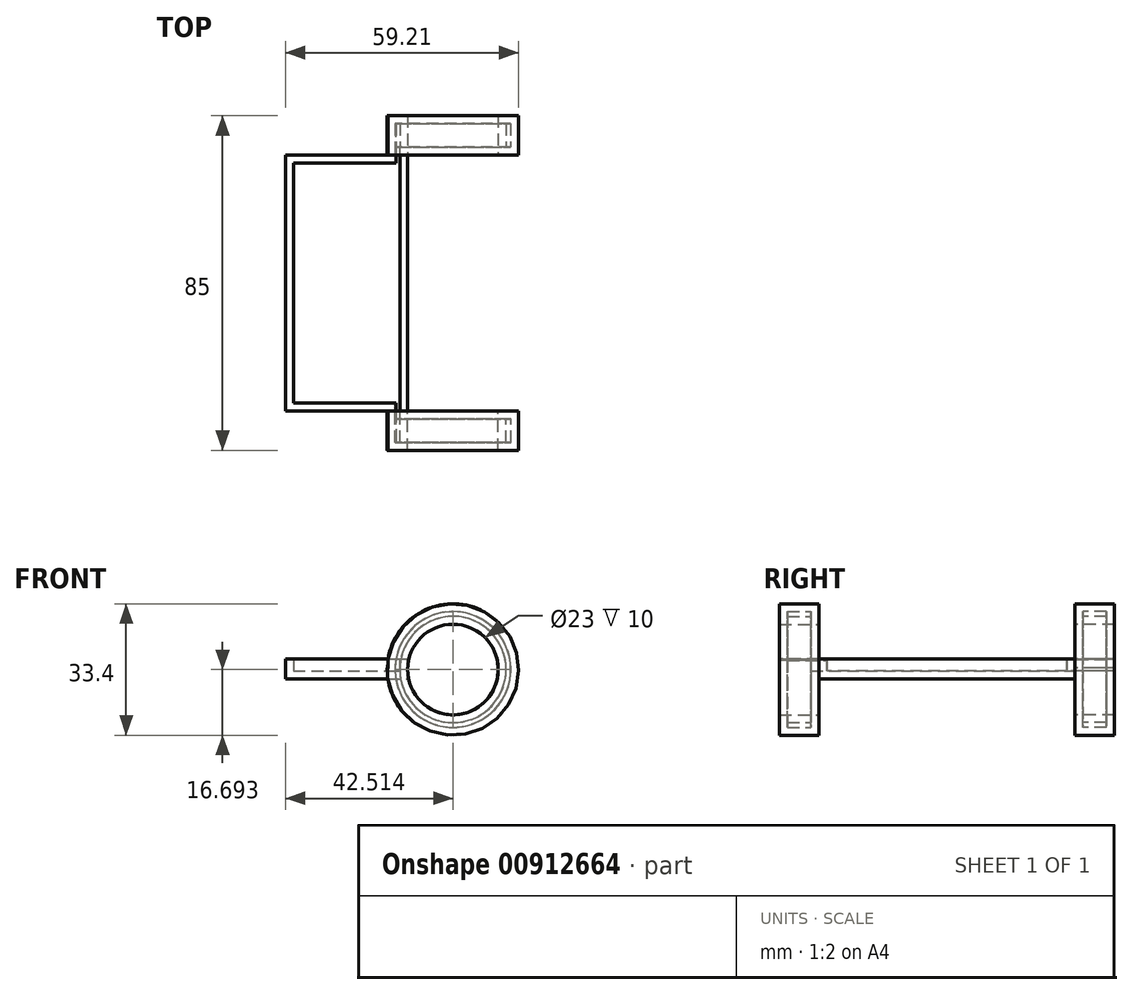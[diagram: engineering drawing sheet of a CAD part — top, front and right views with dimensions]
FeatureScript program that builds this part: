
annotation { "Feature Type Name" : "Feature", "Feature Type Description" : "" }
export const myFeature = defineFeature(function(context is Context, id is Id, definition is map)
    precondition{}
    {
        {
            var Q0;
            Q0=qCreatedBy(makeId("Top.planeOp"),FACE);
            var sketch = newSketch(context, id + "F0", { "sketchPlane" : qUnion([Q0])});
            skLineSegment(sketch, "E0.bottom", {"start": v(-43.57, 32.5) * mm, "end": v(-12.57, 32.5) * mm});
            skLineSegment(sketch, "E0.top", {"start": v(-43.57, -32.5) * mm, "end": v(-12.57, -32.5) * mm});
            skLineSegment(sketch, "E0.left", {"start": v(-43.57, 32.5) * mm, "end": v(-43.57, -32.5) * mm});
            skLineSegment(sketch, "E0.right", {"start": v(-12.57, 32.5) * mm, "end": v(-12.57, -32.5) * mm});
            skLineSegment(sketch, "E1.bottom", {"start": v(-12.57, -32.5) * mm, "end": v(-17.57, -32.5) * mm});
            skLineSegment(sketch, "E1.top", {"start": v(-12.57, -42.5) * mm, "end": v(-17.57, -42.5) * mm});
            skLineSegment(sketch, "E1.left", {"start": v(-12.57, -32.5) * mm, "end": v(-12.57, -42.5) * mm});
            skLineSegment(sketch, "E1.right", {"start": v(-17.57, -32.5) * mm, "end": v(-17.57, -42.5) * mm});
            skLineSegment(sketch, "E2.bottom", {"start": v(-12.57, 32.5) * mm, "end": v(-17.57, 32.5) * mm});
            skLineSegment(sketch, "E2.top", {"start": v(-12.57, 42.5) * mm, "end": v(-17.57, 42.5) * mm});
            skLineSegment(sketch, "E2.left", {"start": v(-12.57, 32.5) * mm, "end": v(-12.57, 42.5) * mm});
            skLineSegment(sketch, "E2.right", {"start": v(-17.57, 32.5) * mm, "end": v(-17.57, 42.5) * mm});
            skLineSegment(sketch, "E3", {"start": v(-43.57, 0) * mm, "end": v(-65.23, 0) * mm});
            skLineSegment(sketch, "E4", {"start": v(-17.57, 32.5) * mm, "end": v(-12.57, 32.5) * mm});
            skLineSegment(sketch, "E5", {"start": v(-17.57, -32.5) * mm, "end": v(-12.57, -32.5) * mm});
            skSolve(sketch);
        }
        {
            var Q0;
            Q0 = qSketchRegion(id + "F0", true);
            var Q1;
            Q1=makeQuery(id+"F0.imprint","IMPRINT",FACE,{"disambiguationData":[TD([[makeQuery(id+"F0.imprint","IMPRINT",EDGE,{"derivedFrom":sQuery(id+"F0.wireOp",EDGE,"E0.bottom")}),-1.0]])]});
            extrude(context, id + "F1", {"entities" : qUnion([Q0, Q1]), "depth" : 5 * mm, "offsetDistance" : 25.4 * mm});
        }
        {
            var Q0;
            Q0=qCreatedBy(makeId("Front.planeOp"),FACE);
            cPlane(context, id + "F2", {"entities" : qUnion([Q0]), "cplaneType" : CPlaneType.OFFSET, "offset" : 32.5 * mm, "width" : 152.4 * mm, "height" : 152.4 * mm});
        }
        {
            var Q0;
            Q0=qCreatedBy(makeId("Front.planeOp"),FACE);
            cPlane(context, id + "F3", {"entities" : qUnion([Q0]), "cplaneType" : CPlaneType.OFFSET, "offset" : 32.5 * mm, "oppositeDirection" : true, "width" : 152.4 * mm, "height" : 152.4 * mm});
        }
        {
            var Q0;
            Q0=qCreatedBy(id+"F3.planeOp",FACE);
            var sketch = newSketch(context, id + "F4", { "sketchPlane" : qUnion([Q0])});
            skCircle(sketch, "E6", {"center": v(-1.07, 2.34) * mm, "radius": 16.7 * mm});
            skCircle(sketch, "E7", {"center": v(-1.07, 2.34) * mm, "radius": 11.5 * mm});
            skSolve(sketch);
        }
        {
            var Q0;
            Q0 = qSketchRegion(id + "F4", true);
            extrude(context, id + "F5", {"entities" : qUnion([Q0]), "operationType" : NewBodyOperationType.ADD, "oppositeDirection" : true, "depth" : 10 * mm, "offsetDistance" : 25.4 * mm});
        }
        {
            var Q0;
            Q0=qCreatedBy(id+"F2.planeOp",FACE);
            var sketch = newSketch(context, id + "F6", { "sketchPlane" : qUnion([Q0])});
            skCircle(sketch, "E8", {"center": v(-1.06, 2.33) * mm, "radius": 11.5 * mm});
            skCircle(sketch, "E9", {"center": v(-1.06, 2.33) * mm, "radius": 16.7 * mm});
            skSolve(sketch);
        }
        {
            var Q0;
            Q0 = qSketchRegion(id + "F6", true);
            extrude(context, id + "F7", {"entities" : qUnion([Q0]), "operationType" : NewBodyOperationType.ADD, "depth" : 10 * mm, "offsetDistance" : 25.4 * mm});
        }
        {
            var Q0;
            Q0=makeQuery(id+"F1.opExtrude","CAP_FACE",FACE,{"disambiguationData":[OSD([sQuery(id+"F0.wireOp",EDGE,"E0.bottom"),sQuery(id+"F0.wireOp",EDGE,"E0.top"),sQuery(id+"F0.wireOp",EDGE,"E0.left"),sQuery(id+"F0.wireOp",EDGE,"E0.right"),sQuery(id+"F0.wireOp",EDGE,"E1.top"),sQuery(id+"F0.wireOp",EDGE,"E1.left"),sQuery(id+"F0.wireOp",EDGE,"E1.right"),sQuery(id+"F0.wireOp",EDGE,"E2.top"),sQuery(id+"F0.wireOp",EDGE,"E2.left"),sQuery(id+"F0.wireOp",EDGE,"E2.right")])],"isStart":false});
            shell(context, id + "F8", {"entities" : qUnion([Q0]), "thickness" : 2 * mm});
        }
    });
